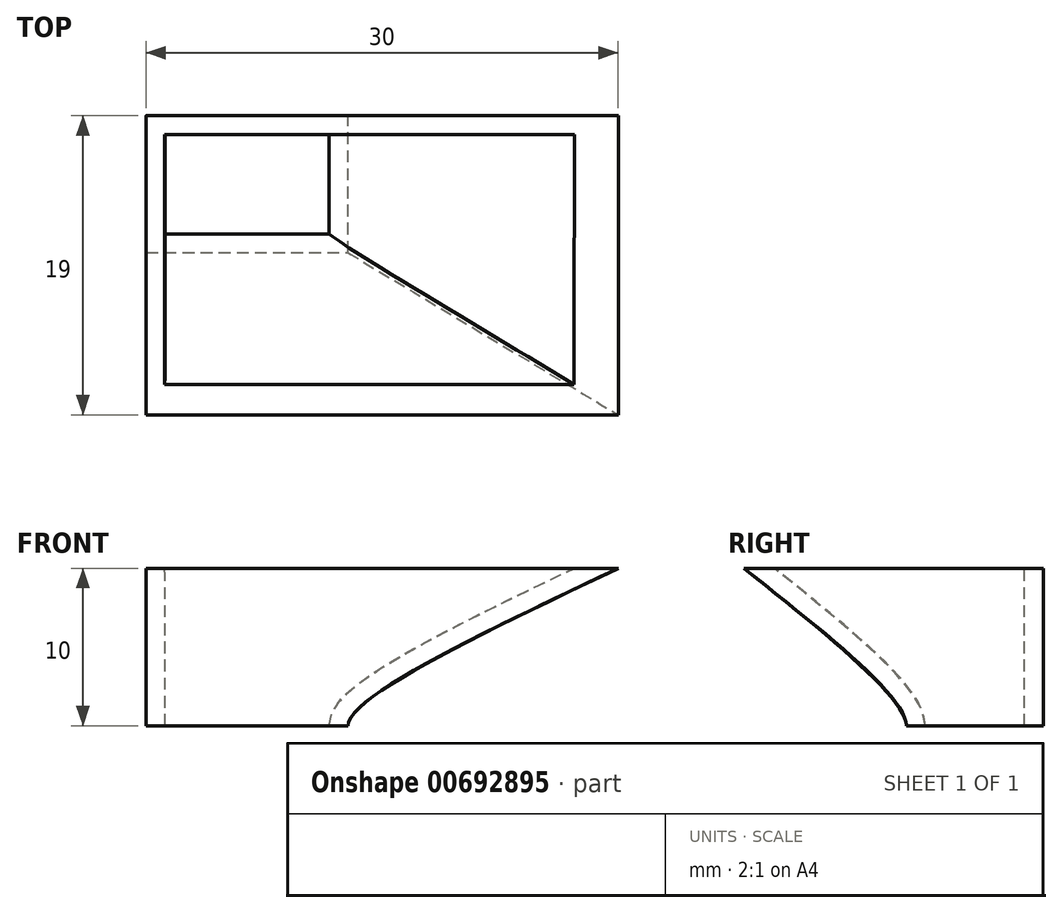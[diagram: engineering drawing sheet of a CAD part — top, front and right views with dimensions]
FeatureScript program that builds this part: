
annotation { "Feature Type Name" : "Feature", "Feature Type Description" : "" }
export const myFeature = defineFeature(function(context is Context, id is Id, definition is map)
    precondition{}
    {
        {
            var Q0;
            Q0=qCreatedBy(makeId("Top.planeOp"),FACE);
            var sketch = newSketch(context, id + "F0", { "sketchPlane" : qUnion([Q0])});
            skLineSegment(sketch, "E0.bottom", {"start": v(0, 0) * mm, "end": v(12.8, 0) * mm});
            skLineSegment(sketch, "E0.top", {"start": v(0, 8.7) * mm, "end": v(12.8, 8.7) * mm});
            skLineSegment(sketch, "E0.left", {"start": v(0, 0) * mm, "end": v(0, 8.7) * mm});
            skLineSegment(sketch, "E0.right", {"start": v(12.8, 0) * mm, "end": v(12.8, 8.7) * mm});
            skSolve(sketch);
        }
        {
            var Q0;
            Q0=qCreatedBy(makeId("Top.planeOp"),FACE);
            cPlane(context, id + "F1", {"entities" : qUnion([Q0]), "cplaneType" : CPlaneType.OFFSET, "offset" : 10 * mm, "width" : 150 * mm, "height" : 150 * mm});
        }
        {
            var Q0;
            Q0=qCreatedBy(id+"F1.planeOp",FACE);
            var sketch = newSketch(context, id + "F2", { "sketchPlane" : qUnion([Q0])});
            skLineSegment(sketch, "E1.bottom", {"start": v(29.97, -10.3) * mm, "end": v(-0.03, -10.3) * mm});
            skLineSegment(sketch, "E1.top", {"start": v(29.97, 8.7) * mm, "end": v(-0.03, 8.7) * mm});
            skLineSegment(sketch, "E1.left", {"start": v(29.97, -10.3) * mm, "end": v(29.97, 8.7) * mm});
            skLineSegment(sketch, "E1.right", {"start": v(-0.03, -10.3) * mm, "end": v(-0.03, 8.7) * mm});
            skPoint(sketch, "E1.middle", {"position": v(14.97, -0.8) * mm});
            skSolve(sketch);
        }
        {
            var Q0;
            Q0=makeQuery(id+"F0.imprint","IMPRINT",FACE,{"disambiguationData":[TD([[makeQuery(id+"F0.imprint","IMPRINT",EDGE,{"derivedFrom":sQuery(id+"F0.wireOp",EDGE,"E0.bottom")}),1.0]])]});
            var Q1;
            Q1=makeQuery(id+"F2.imprint","IMPRINT",FACE,{"disambiguationData":[TD([[makeQuery(id+"F2.imprint","IMPRINT",EDGE,{"derivedFrom":sQuery(id+"F2.wireOp",EDGE,"E1.bottom")}),-1.0]])]});
            var Q2;
            Q2=sQuery(id+"F0.wireOp",VERTEX,"E0.bottom.start");
            var Q3;
            Q3=sQuery(id+"F2.wireOp",VERTEX,"E1.right.start");
            loft(context, id + "F3", {"startCondition" : LoftEndDerivativeType.NORMAL_TO_PROFILE, "startMagnitude" : 0.5, "sheetProfilesArray" : [{ "sheetProfileEntities" : qUnion([Q0]) }, { "sheetProfileEntities" : qUnion([Q1]) }], "matchConnections" : true, "connections" : [{ "connectionEntities" : qUnion([Q2, Q3]), "connectionEdgeQueries" : qUnion([]), "connectionEdgeParameters" : [] }]});
        }
        {
            var Q0;
            Q0=makeQuery(id+"F3.opLoft","CAP_FACE",FACE,{"disambiguationData":[OSD([makeQuery(id+"F2.imprint","IMPRINT",FACE,{"disambiguationData":[TD([[makeQuery(id+"F2.imprint","IMPRINT",EDGE,{"derivedFrom":sQuery(id+"F2.wireOp",EDGE,"E1.bottom")}),-1.0]])]})])],"isStart":true});
            var Q1;
            Q1=makeQuery(id+"F3.opLoft","CAP_FACE",FACE,{"disambiguationData":[OSD([makeQuery(id+"F0.imprint","IMPRINT",FACE,{"disambiguationData":[TD([[makeQuery(id+"F0.imprint","IMPRINT",EDGE,{"derivedFrom":sQuery(id+"F0.wireOp",EDGE,"E0.bottom")}),1.0]])]})])],"isStart":true});
            shell(context, id + "F4", {"entities" : qUnion([Q0, Q1]), "thickness" : 1.2 * mm});
        }
    });
